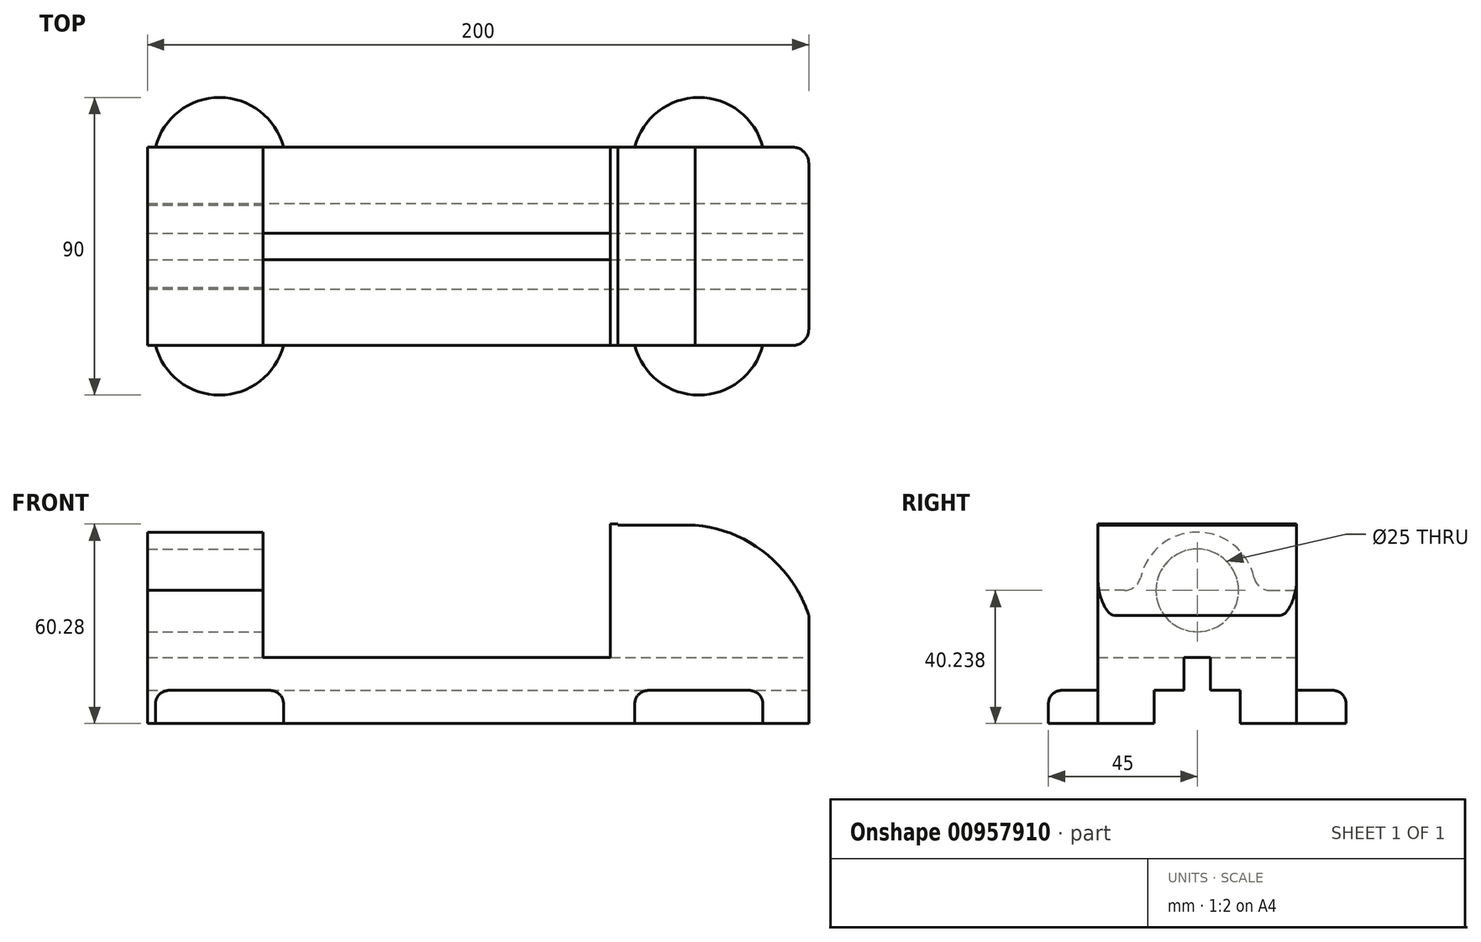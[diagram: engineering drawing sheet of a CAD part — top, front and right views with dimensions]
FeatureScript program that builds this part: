
annotation { "Feature Type Name" : "Feature", "Feature Type Description" : "" }
export const myFeature = defineFeature(function(context is Context, id is Id, definition is map)
    precondition{}
    {
        {
            var Q0;
            Q0=qCreatedBy(makeId("Front.planeOp"),FACE);
            var sketch = newSketch(context, id + "F0", { "sketchPlane" : qUnion([Q0])});
            skLineSegment(sketch, "E0", {"start": v(-56.17, -26.37) * mm, "end": v(143.83, -26.37) * mm});
            skLineSegment(sketch, "E1", {"start": v(143.83, -26.37) * mm, "end": v(143.83, 33.63) * mm});
            skLineSegment(sketch, "E2", {"start": v(83.83, 33.63) * mm, "end": v(143.83, 33.63) * mm});
            skLineSegment(sketch, "E3", {"start": v(83.83, 33.63) * mm, "end": v(83.83, -6.37) * mm});
            skLineSegment(sketch, "E4", {"start": v(83.83, -6.37) * mm, "end": v(3.83, -6.37) * mm});
            skLineSegment(sketch, "E5", {"start": v(3.83, -6.37) * mm, "end": v(3.83, 33.63) * mm});
            skLineSegment(sketch, "E6", {"start": v(3.83, 33.63) * mm, "end": v(-56.17, 33.63) * mm});
            skLineSegment(sketch, "E7", {"start": v(-56.17, 33.63) * mm, "end": v(-56.17, -26.37) * mm});
            skSolve(sketch);
        }
        {
            var Q0;
            Q0=makeQuery(id+"F0.imprint","IMPRINT",FACE,{"disambiguationData":[TD([[makeQuery(id+"F0.imprint","IMPRINT",EDGE,{"derivedFrom":sQuery(id+"F0.wireOp",EDGE,"E0")}),1.0]])]});
            extrude(context, id + "F1", {"entities" : qUnion([Q0]), "depth" : 60 * mm, "offsetDistance" : 25 * mm});
        }
        {
            var Q0;
            Q0=qCreatedBy(makeId("Right.planeOp"),FACE);
            var sketch = newSketch(context, id + "F2", { "sketchPlane" : qUnion([Q0])});
            skCircle(sketch, "E8", {"center": v(-30, 13.87) * mm, "radius": 12.5 * mm});
            skSolve(sketch);
        }
        {
            var Q0;
            Q0 = qSketchRegion(id + "F2", true);
            extrude(context, id + "F3", {"entities" : qUnion([Q0]), "operationType" : NewBodyOperationType.REMOVE, "oppositeDirection" : true, "depth" : 60 * mm, "offsetDistance" : 25 * mm});
        }
        {
            var Q0;
            Q0=makeQuery(id+"F1.opExtrude","SWEPT_FACE",FACE,{"disambiguationData":[OSD([sQuery(id+"F0.wireOp",EDGE,"E0")])]});
            var sketch = newSketch(context, id + "F4", { "sketchPlane" : qUnion([Q0])});
            skArc(sketch, "E9", {"start": v(-54.4, 5) * mm, "mid": v(-34.4, -15) * mm, "end": v(-14.4, 5) * mm});
            skArc(sketch, "E10", {"start": v(90.57, 5) * mm, "mid": v(110.57, -15) * mm, "end": v(130.57, 5) * mm});
            skArc(sketch, "E11", {"start": v(130.57, 55) * mm, "mid": v(110.57, 75) * mm, "end": v(90.57, 55) * mm});
            skArc(sketch, "E12", {"start": v(-14.4, 55) * mm, "mid": v(-34.4, 75) * mm, "end": v(-54.4, 55) * mm});
            skSolve(sketch);
        }
        {
            var Q0;
            {var subQ0=sQuery(id+"F4.wireOp",EDGE,"E12");var subQ1=makeQuery(id+"F1.opExtrude","CAP_EDGE",EDGE,{"disambiguationData":[OSD([sQuery(id+"F0.wireOp",EDGE,"E0")])],"isStart":false});var subQ2=makeQuery(id+"F4.imprint","INTERSECT",VERTEX,{"disambiguationData":[OD(0.0)],"derivedFrom":[subQ1,subQ0]});Q0=makeQuery(id+"F4.imprint","IMPRINT",FACE,{"disambiguationData":[TD([[makeQuery(id+"F4.imprint","IMPRINT",EDGE,{"disambiguationData":[TD([[subQ2,1.0]])],"derivedFrom":subQ0}),1.0]])]});}
            var Q1;
            {var subQ0=sQuery(id+"F4.wireOp",EDGE,"E11");var subQ1=makeQuery(id+"F1.opExtrude","CAP_EDGE",EDGE,{"disambiguationData":[OSD([sQuery(id+"F0.wireOp",EDGE,"E0")])],"isStart":false});var subQ2=makeQuery(id+"F4.imprint","INTERSECT",VERTEX,{"disambiguationData":[OD(0.0)],"derivedFrom":[subQ1,subQ0]});Q1=makeQuery(id+"F4.imprint","IMPRINT",FACE,{"disambiguationData":[TD([[makeQuery(id+"F4.imprint","IMPRINT",EDGE,{"disambiguationData":[TD([[subQ2,-1.0]])],"derivedFrom":subQ0}),1.0]])]});}
            var Q2;
            {var subQ0=sQuery(id+"F4.wireOp",EDGE,"E9");var subQ1=makeQuery(id+"F1.opExtrude","CAP_EDGE",EDGE,{"disambiguationData":[OSD([sQuery(id+"F0.wireOp",EDGE,"E0")])],"isStart":true});var subQ2=makeQuery(id+"F4.imprint","INTERSECT",VERTEX,{"disambiguationData":[OD(0.0)],"derivedFrom":[subQ1,subQ0]});Q2=makeQuery(id+"F4.imprint","IMPRINT",FACE,{"disambiguationData":[TD([[makeQuery(id+"F4.imprint","IMPRINT",EDGE,{"disambiguationData":[TD([[subQ2,-1.0]])],"derivedFrom":subQ0}),1.0]])]});}
            var Q3;
            {var subQ0=sQuery(id+"F4.wireOp",EDGE,"E10");var subQ1=makeQuery(id+"F1.opExtrude","CAP_EDGE",EDGE,{"disambiguationData":[OSD([sQuery(id+"F0.wireOp",EDGE,"E0")])],"isStart":true});var subQ2=makeQuery(id+"F4.imprint","INTERSECT",VERTEX,{"disambiguationData":[OD(0.0)],"derivedFrom":[subQ1,subQ0]});Q3=makeQuery(id+"F4.imprint","IMPRINT",FACE,{"disambiguationData":[TD([[makeQuery(id+"F4.imprint","IMPRINT",EDGE,{"disambiguationData":[TD([[subQ2,1.0]])],"derivedFrom":subQ0}),1.0]])]});}
            extrude(context, id + "F5", {"entities" : qUnion([Q0, Q1, Q2, Q3]), "oppositeDirection" : true, "depth" : 10 * mm, "offsetDistance" : 25 * mm});
        }
        {
            var Q0;
            Q0=makeQuery(id+"F1.opExtrude","CAP_FACE",FACE,{"disambiguationData":[OSD([sQuery(id+"F0.wireOp",EDGE,"E0"),sQuery(id+"F0.wireOp",EDGE,"E1"),sQuery(id+"F0.wireOp",EDGE,"E2"),sQuery(id+"F0.wireOp",EDGE,"E3"),sQuery(id+"F0.wireOp",EDGE,"E4"),sQuery(id+"F0.wireOp",EDGE,"E5"),sQuery(id+"F0.wireOp",EDGE,"E6"),sQuery(id+"F0.wireOp",EDGE,"E7")])],"isStart":false});
            var sketch = newSketch(context, id + "F6", { "sketchPlane" : qUnion([Q0])});
            skArc(sketch, "E13", {"start": v(143.83, 6.27) * mm, "mid": v(127.79, 27.23) * mm, "end": v(102.17, 33.63) * mm});
            skSolve(sketch);
        }
        {
            var Q0;
            {var subQ0=sQuery(id+"F6.wireOp",EDGE,"E13");var subQ1=makeQuery(id+"F1.opExtrude","CAP_EDGE",EDGE,{"disambiguationData":[OSD([sQuery(id+"F0.wireOp",EDGE,"E1")])],"isStart":false});var subQ2=makeQuery(id+"F6.imprint","INTERSECT",VERTEX,{"derivedFrom":[subQ1,subQ0]});Q0=makeQuery(id+"F6.imprint","IMPRINT",FACE,{"disambiguationData":[TD([[makeQuery(id+"F6.imprint","IMPRINT",EDGE,{"disambiguationData":[TD([[subQ2,-1.0]])],"derivedFrom":subQ0}),-1.0]])]});}
            extrude(context, id + "F7", {"entities" : qUnion([Q0]), "operationType" : NewBodyOperationType.REMOVE, "oppositeDirection" : true, "depth" : 157 * mm, "offsetDistance" : 25 * mm});
        }
        {
            var Q0;
            Q0=makeQuery(id+"F1.opExtrude","CAP_EDGE",EDGE,{"disambiguationData":[OSD([sQuery(id+"F0.wireOp",EDGE,"E1")])],"isStart":false});
            var Q1;
            Q1=makeQuery(id+"F1.opExtrude","CAP_EDGE",EDGE,{"disambiguationData":[OSD([sQuery(id+"F0.wireOp",EDGE,"E1")])],"isStart":true});
            var Q2;
            Q2=makeQuery(id+"F7.boolean.opBoolean","COPY",EDGE,{"derivedFrom":makeQuery(id+"F7.opExtrude","SWEPT_EDGE",EDGE,{"disambiguationData":[OSD([sQuery(id+"F0.wireOp",EDGE,"E1"),sQuery(id+"F6.wireOp",EDGE,"E13")])]})});
            fillet(context, id + "F8", {"entities" : qUnion([Q0, Q1, Q2]), "radius" : 5 * mm, "tangentPropagation" : true, "allowEdgeOverflow" : false});
        }
        {
            var Q0;
            Q0=makeQuery(id+"F1.opExtrude","SWEPT_FACE",FACE,{"disambiguationData":[OSD([sQuery(id+"F0.wireOp",EDGE,"E1")])]});
            var sketch = newSketch(context, id + "F9", { "sketchPlane" : qUnion([Q0])});
            skLineSegment(sketch, "E14", {"start": v(-43, -26.37) * mm, "end": v(-5, -26.37) * mm});
            skLineSegment(sketch, "E15", {"start": v(-17, -26.37) * mm, "end": v(-17, -16.37) * mm});
            skLineSegment(sketch, "E16", {"start": v(-43, -26.37) * mm, "end": v(-43, -16.37) * mm});
            skLineSegment(sketch, "E17", {"start": v(-43, -16.37) * mm, "end": v(-34, -16.37) * mm});
            skLineSegment(sketch, "E18", {"start": v(-17, -16.37) * mm, "end": v(-26, -16.37) * mm});
            skLineSegment(sketch, "E19", {"start": v(-26, -16.37) * mm, "end": v(-26, -6.37) * mm});
            skLineSegment(sketch, "E20", {"start": v(-26, -6.37) * mm, "end": v(-34, -6.37) * mm});
            skLineSegment(sketch, "E21", {"start": v(-34, -6.37) * mm, "end": v(-34, -16.37) * mm});
            skSolve(sketch);
        }
        {
            var Q0;
            {var subQ1=sQuery(id+"F9.wireOp",EDGE,"E15");Q0=makeQuery(id+"F9.imprint","IMPRINT",FACE,{"disambiguationData":[TD([[makeQuery(id+"F9.imprint","IMPRINT",EDGE,{"derivedFrom":subQ1}),1.0]])]});}
            extrude(context, id + "F10", {"entities" : qUnion([Q0]), "operationType" : NewBodyOperationType.REMOVE, "oppositeDirection" : true, "depth" : 295 * mm, "offsetDistance" : 25 * mm});
        }
        {
            var Q0;
            Q0=makeQuery(id+"F1.opExtrude","SWEPT_FACE",FACE,{"disambiguationData":[OSD([sQuery(id+"F0.wireOp",EDGE,"E7")])]});
            var sketch = newSketch(context, id + "F11", { "sketchPlane" : qUnion([Q0])});
            skArc(sketch, "E22", {"start": v(47.6, 13.87) * mm, "mid": v(30, 31.47) * mm, "end": v(12.4, 13.87) * mm});
            skLineSegment(sketch, "E23", {"start": v(47.6, 13.87) * mm, "end": v(60, 13.87) * mm});
            skLineSegment(sketch, "E24", {"start": v(12.4, 13.87) * mm, "end": v(0, 13.87) * mm});
            skSolve(sketch);
        }
        {
            var Q0;
            Q0=makeQuery(id+"F11.imprint","IMPRINT",FACE,{"disambiguationData":[TD([[makeQuery(id+"F11.imprint","IMPRINT",EDGE,{"derivedFrom":sQuery(id+"F11.wireOp",EDGE,"E22")}),-1.0]])]});
            extrude(context, id + "F12", {"entities" : qUnion([Q0]), "operationType" : NewBodyOperationType.REMOVE, "oppositeDirection" : true, "depth" : 111 * mm, "offsetDistance" : 25 * mm});
        }
        {
            var Q0;
            Q0=makeQuery(id+"F1.opExtrude","SWEPT_FACE",FACE,{"disambiguationData":[OSD([sQuery(id+"F0.wireOp",EDGE,"E5")])]});
            extrude(context, id + "F13", {"entities" : qUnion([Q0]), "operationType" : NewBodyOperationType.REMOVE, "oppositeDirection" : true, "depth" : 25 * mm, "offsetDistance" : 25 * mm});
        }
        {
            var Q0;
            Q0=makeQuery(id+"F12.boolean.opBoolean","COPY",EDGE,{"derivedFrom":makeQuery(id+"F12.opExtrude","SWEPT_EDGE",EDGE,{"disambiguationData":[OSD([sQuery(id+"F11.wireOp",EDGE,"E22"),sQuery(id+"F11.wireOp",EDGE,"E23")])]})});
            fillet(context, id + "F14", {"entities" : qUnion([Q0]), "radius" : 5 * mm, "tangentPropagation" : true, "allowEdgeOverflow" : false});
        }
        {
            var Q0;
            Q0=makeQuery(id+"F12.boolean.opBoolean","COPY",EDGE,{"derivedFrom":makeQuery(id+"F12.opExtrude","SWEPT_EDGE",EDGE,{"disambiguationData":[OSD([sQuery(id+"F11.wireOp",EDGE,"E22"),sQuery(id+"F11.wireOp",EDGE,"E24")])]})});
            fillet(context, id + "F15", {"entities" : qUnion([Q0]), "radius" : 5 * mm, "tangentPropagation" : true, "allowEdgeOverflow" : false});
        }
        {
            var Q0;
            Q0=makeQuery(id+"F5.opExtrude","CAP_EDGE",EDGE,{"disambiguationData":[OSD([sQuery(id+"F4.wireOp",EDGE,"E12")])],"isStart":false});
            fillet(context, id + "F16", {"entities" : qUnion([Q0]), "radius" : 4 * mm, "tangentPropagation" : true, "allowEdgeOverflow" : false});
        }
        {
            var Q0;
            Q0=makeQuery(id+"F5.opExtrude","CAP_EDGE",EDGE,{"disambiguationData":[OSD([sQuery(id+"F4.wireOp",EDGE,"E11")])],"isStart":false});
            fillet(context, id + "F17", {"entities" : qUnion([Q0]), "radius" : 4 * mm, "tangentPropagation" : true, "allowEdgeOverflow" : false});
        }
        {
            var Q0;
            Q0=makeQuery(id+"F5.opExtrude","CAP_EDGE",EDGE,{"disambiguationData":[OSD([sQuery(id+"F4.wireOp",EDGE,"E9")])],"isStart":false});
            var Q1;
            Q1=makeQuery(id+"F5.opExtrude","CAP_EDGE",EDGE,{"disambiguationData":[OSD([sQuery(id+"F4.wireOp",EDGE,"E10")])],"isStart":false});
            fillet(context, id + "F18", {"entities" : qUnion([Q0, Q1]), "radius" : 4 * mm, "tangentPropagation" : true, "allowEdgeOverflow" : false});
        }
        {
            var Q0;
            Q0=makeQuery(id+"F1.opExtrude","SWEPT_FACE",FACE,{"disambiguationData":[OSD([sQuery(id+"F0.wireOp",EDGE,"E2")])]});
            var sketch = newSketch(context, id + "F19", { "sketchPlane" : qUnion([Q0])});
            skLineSegment(sketch, "E25.bottom", {"start": v(83.83, -60) * mm, "end": v(86.07, -60) * mm});
            skLineSegment(sketch, "E25.top", {"start": v(83.83, 0) * mm, "end": v(86.07, 0) * mm});
            skLineSegment(sketch, "E25.left", {"start": v(83.83, -60) * mm, "end": v(83.83, 0) * mm});
            skLineSegment(sketch, "E26", {"start": v(86.07, 0) * mm, "end": v(86.07, -60) * mm});
            skSolve(sketch);
        }
        {
            var Q0;
            Q0=makeQuery(id+"F19.imprint","IMPRINT",FACE,{"disambiguationData":[TD([[makeQuery(id+"F19.imprint","IMPRINT",EDGE,{"derivedFrom":sQuery(id+"F19.wireOp",EDGE,"E25.bottom")}),1.0]])]});
            extrude(context, id + "F20", {"entities" : qUnion([Q0]), "operationType" : NewBodyOperationType.ADD, "depth" : 0.28 * mm, "offsetDistance" : 25 * mm});
        }
    });
